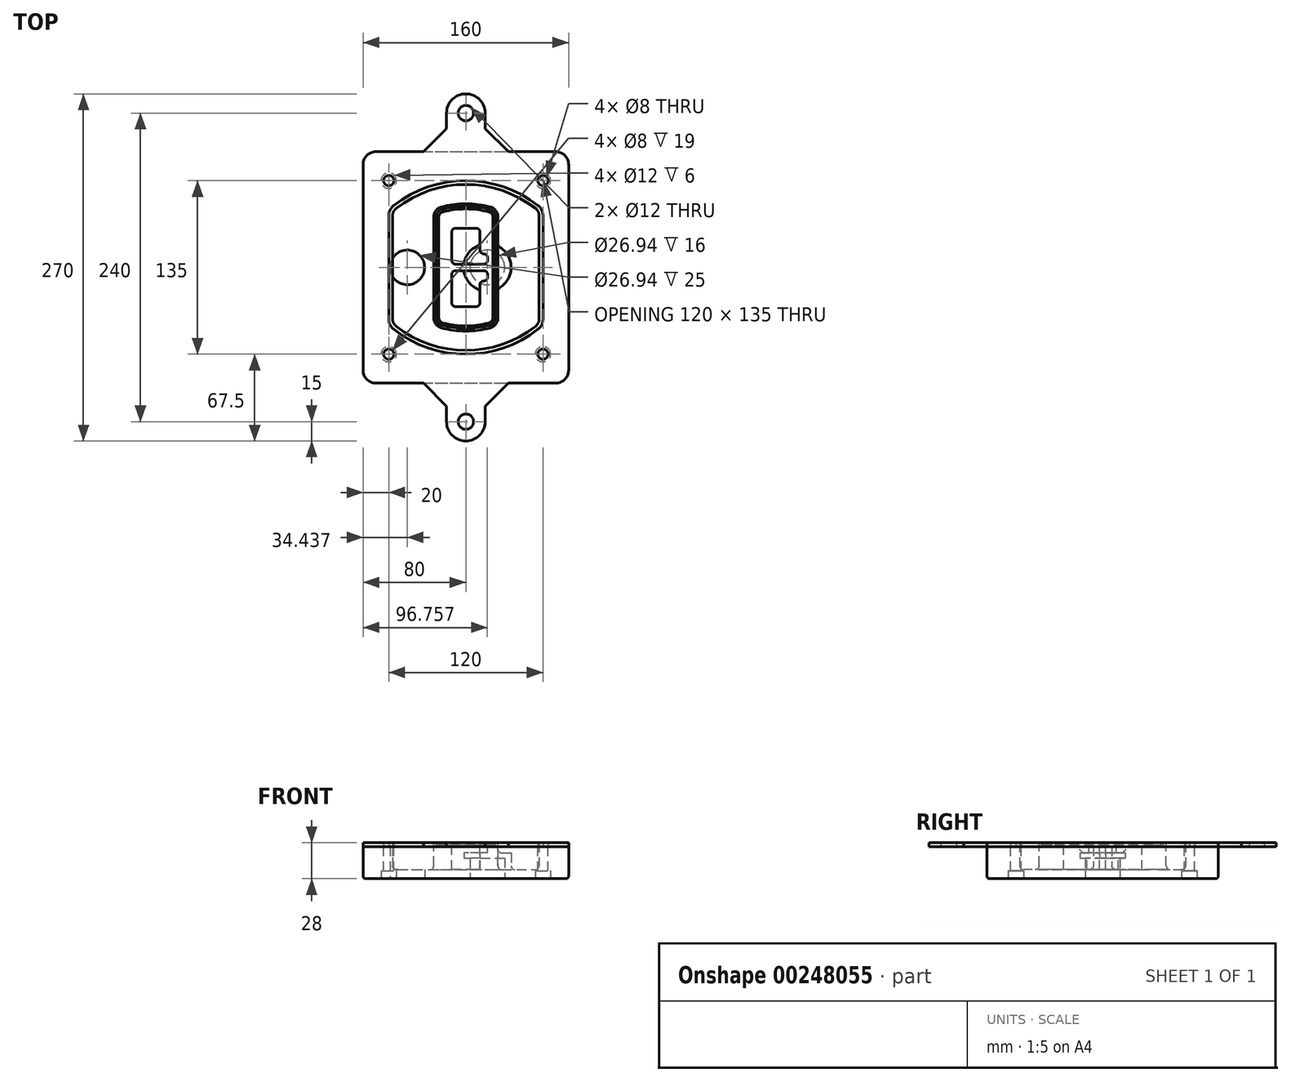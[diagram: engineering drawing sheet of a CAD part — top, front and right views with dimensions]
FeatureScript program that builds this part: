
annotation { "Feature Type Name" : "Feature", "Feature Type Description" : "" }
export const myFeature = defineFeature(function(context is Context, id is Id, definition is map)
    precondition{}
    {
        {
            var Q0;
            Q0=qCreatedBy(makeId("Top.planeOp"),FACE);
            var sketch = newSketch(context, id + "F0", { "sketchPlane" : qUnion([Q0])});
            skPoint(sketch, "E0.rect.middle", {"position": v(0, 0) * mm});
            skLineSegment(sketch, "E1.bottom", {"start": v(-70, -90) * mm, "end": v(70, -90) * mm});
            skLineSegment(sketch, "E1.top", {"start": v(-70, 90) * mm, "end": v(70, 90) * mm});
            skLineSegment(sketch, "E1.left", {"start": v(-80, -80) * mm, "end": v(-80, 80) * mm});
            skLineSegment(sketch, "E1.right", {"start": v(80, -80) * mm, "end": v(80, 80) * mm});
            skLineSegment(sketch, "E2", {"start": v(-80, 90) * mm, "end": v(80, -90) * mm, "construction": true});
            skLineSegment(sketch, "E3", {"start": v(80, 90) * mm, "end": v(-80, -90) * mm, "construction": true});
            skCircle(sketch, "E4", {"center": v(-60, 67.5) * mm, "radius": 4 * mm});
            skCircle(sketch, "E5", {"center": v(60, 67.5) * mm, "radius": 4 * mm});
            skCircle(sketch, "E6", {"center": v(60, -67.5) * mm, "radius": 4 * mm});
            skCircle(sketch, "E7", {"center": v(-60, -67.5) * mm, "radius": 4 * mm});
            skLineSegment(sketch, "E8", {"start": v(-60, 67.5) * mm, "end": v(60, 67.5) * mm, "construction": true});
            skLineSegment(sketch, "E9", {"start": v(60, 67.5) * mm, "end": v(60, -67.5) * mm, "construction": true});
            skLineSegment(sketch, "E10", {"start": v(60, -67.5) * mm, "end": v(-60, -67.5) * mm, "construction": true});
            skLineSegment(sketch, "E11", {"start": v(-60, -67.5) * mm, "end": v(-60, 67.5) * mm, "construction": true});
            skLineSegment(sketch, "E12", {"start": v(-60, 40.3) * mm, "end": v(-60, -40.3) * mm});
            skLineSegment(sketch, "E13", {"start": v(60, 40.3) * mm, "end": v(60, -40.3) * mm});
            skArc(sketch, "E14", {"start": v(56.15, 48.18) * mm, "mid": v(0, 67.5) * mm, "end": v(-56.15, 48.18) * mm});
            skArc(sketch, "E15", {"start": v(-56.15, -48.18) * mm, "mid": v(0, -67.5) * mm, "end": v(56.15, -48.18) * mm});
            skLineSegment(sketch, "E16", {"start": v(-60, 0) * mm, "end": v(60, 0) * mm, "construction": true});
            skPoint(sketch, "E17.visualSharp", {"position": v(-60, -45) * mm});
            skArc(sketch, "E17.filletArc", {"start": v(-60, -40.3) * mm, "mid": v(-58.99, -44.68) * mm, "end": v(-56.15, -48.18) * mm});
            skPoint(sketch, "E18.visualSharp", {"position": v(-60, 45) * mm});
            skArc(sketch, "E18.filletArc", {"start": v(-56.15, 48.18) * mm, "mid": v(-58.99, 44.68) * mm, "end": v(-60, 40.3) * mm});
            skPoint(sketch, "E19.visualSharp", {"position": v(60, 45) * mm});
            skArc(sketch, "E19.filletArc", {"start": v(60, 40.3) * mm, "mid": v(58.99, 44.68) * mm, "end": v(56.15, 48.18) * mm});
            skPoint(sketch, "E20.visualSharp", {"position": v(60, -45) * mm});
            skArc(sketch, "E20.filletArc", {"start": v(56.15, -48.18) * mm, "mid": v(58.99, -44.68) * mm, "end": v(60, -40.3) * mm});
            skPoint(sketch, "E21.visualSharp", {"position": v(-80, 90) * mm});
            skArc(sketch, "E21.filletArc", {"start": v(-70, 90) * mm, "mid": v(-77.07, 87.07) * mm, "end": v(-80, 80) * mm});
            skPoint(sketch, "E22.visualSharp", {"position": v(80, 90) * mm});
            skArc(sketch, "E22.filletArc", {"start": v(80, 80) * mm, "mid": v(77.07, 87.07) * mm, "end": v(70, 90) * mm});
            skPoint(sketch, "E23.visualSharp", {"position": v(80, -90) * mm});
            skArc(sketch, "E23.filletArc", {"start": v(70, -90) * mm, "mid": v(77.07, -87.07) * mm, "end": v(80, -80) * mm});
            skPoint(sketch, "E24.visualSharp", {"position": v(-80, -90) * mm});
            skArc(sketch, "E24.filletArc", {"start": v(-80, -80) * mm, "mid": v(-77.07, -87.07) * mm, "end": v(-70, -90) * mm});
            skArc(sketch, "E25.0", {"start": v(57, 40.3) * mm, "mid": v(56.3, 43.36) * mm, "end": v(54.3, 45.81) * mm});
            skLineSegment(sketch, "E25.1", {"start": v(57, 40.3) * mm, "end": v(57, -40.3) * mm});
            skArc(sketch, "E25.2", {"start": v(54.3, -45.81) * mm, "mid": v(56.3, -43.36) * mm, "end": v(57, -40.3) * mm});
            skArc(sketch, "E25.3", {"start": v(-54.3, -45.81) * mm, "mid": v(0, -64.5) * mm, "end": v(54.3, -45.81) * mm});
            skArc(sketch, "E25.4", {"start": v(-57, -40.3) * mm, "mid": v(-56.3, -43.36) * mm, "end": v(-54.3, -45.81) * mm});
            skArc(sketch, "E25.5", {"start": v(54.3, 45.81) * mm, "mid": v(0, 64.5) * mm, "end": v(-54.3, 45.81) * mm});
            skLineSegment(sketch, "E25.6", {"start": v(-57, 40.3) * mm, "end": v(-57, -40.3) * mm});
            skArc(sketch, "E25.7", {"start": v(-54.3, 45.81) * mm, "mid": v(-56.3, 43.36) * mm, "end": v(-57, 40.3) * mm});
            skArc(sketch, "E26.0", {"start": v(-58.62, 51.33) * mm, "mid": v(-62.58, 46.43) * mm, "end": v(-64, 40.3) * mm});
            skArc(sketch, "E26.1", {"start": v(58.62, 51.33) * mm, "mid": v(0, 71.5) * mm, "end": v(-58.62, 51.33) * mm});
            skArc(sketch, "E26.2", {"start": v(64, 40.3) * mm, "mid": v(62.58, 46.43) * mm, "end": v(58.62, 51.33) * mm});
            skLineSegment(sketch, "E26.3", {"start": v(64, 40.3) * mm, "end": v(64, -40.3) * mm});
            skArc(sketch, "E26.4", {"start": v(58.62, -51.33) * mm, "mid": v(62.58, -46.43) * mm, "end": v(64, -40.3) * mm});
            skLineSegment(sketch, "E26.5", {"start": v(-64, 40.3) * mm, "end": v(-64, -40.3) * mm});
            skArc(sketch, "E26.6", {"start": v(-58.62, -51.33) * mm, "mid": v(0, -71.5) * mm, "end": v(58.62, -51.33) * mm});
            skArc(sketch, "E26.7", {"start": v(-64, -40.3) * mm, "mid": v(-62.58, -46.43) * mm, "end": v(-58.62, -51.33) * mm});
            skSolve(sketch);
        }
        {
            var Q0;
            Q0=makeQuery(id+"F0.imprint","IMPRINT",FACE,{"disambiguationData":[TD([[makeQuery(id+"F0.imprint","IMPRINT",EDGE,{"derivedFrom":sQuery(id+"F0.wireOp",EDGE,"E1.bottom")}),1.0]])]});
            var Q1;
            Q1=makeQuery(id+"F0.imprint","IMPRINT",FACE,{"disambiguationData":[TD([[makeQuery(id+"F0.imprint","IMPRINT",EDGE,{"derivedFrom":sQuery(id+"F0.wireOp",EDGE,"E12")}),1.0]])]});
            var Q2;
            Q2=makeQuery(id+"F0.imprint","IMPRINT",FACE,{"disambiguationData":[TD([[makeQuery(id+"F0.imprint","IMPRINT",EDGE,{"derivedFrom":sQuery(id+"F0.wireOp",EDGE,"E25.0")}),1.0]])]});
            var Q3;
            Q3=makeQuery(id+"F0.imprint","IMPRINT",FACE,{"disambiguationData":[TD([[makeQuery(id+"F0.imprint","IMPRINT",EDGE,{"derivedFrom":sQuery(id+"F0.wireOp",EDGE,"E12")}),-1.0]])]});
            extrude(context, id + "F1", {"entities" : qUnion([Q0, Q1, Q2, Q3]), "oppositeDirection" : true, "depth" : 25 * mm});
        }
        {
            var Q0;
            Q0=makeQuery(id+"F0.imprint","IMPRINT",FACE,{"disambiguationData":[TD([[makeQuery(id+"F0.imprint","IMPRINT",EDGE,{"derivedFrom":sQuery(id+"F0.wireOp",EDGE,"E12")}),1.0]])]});
            extrude(context, id + "F2", {"entities" : qUnion([Q0]), "operationType" : NewBodyOperationType.ADD, "depth" : 3 * mm});
        }
        {
            var Q0;
            Q0=makeQuery(id+"F0.imprint","IMPRINT",FACE,{"disambiguationData":[TD([[makeQuery(id+"F0.imprint","IMPRINT",EDGE,{"derivedFrom":sQuery(id+"F0.wireOp",EDGE,"E25.0")}),1.0]])]});
            extrude(context, id + "F3", {"entities" : qUnion([Q0]), "operationType" : NewBodyOperationType.REMOVE, "oppositeDirection" : true, "depth" : 18 * mm});
        }
        {
            var Q0;
            Q0=makeQuery(id+"F2.opExtrude","CAP_FACE",FACE,{"disambiguationData":[OSD([sQuery(id+"F0.wireOp",EDGE,"E12"),sQuery(id+"F0.wireOp",EDGE,"E13"),sQuery(id+"F0.wireOp",EDGE,"E14"),sQuery(id+"F0.wireOp",EDGE,"E15"),sQuery(id+"F0.wireOp",EDGE,"E17.filletArc"),sQuery(id+"F0.wireOp",EDGE,"E18.filletArc"),sQuery(id+"F0.wireOp",EDGE,"E19.filletArc"),sQuery(id+"F0.wireOp",EDGE,"E20.filletArc"),sQuery(id+"F0.wireOp",EDGE,"E25.0"),sQuery(id+"F0.wireOp",EDGE,"E25.1"),sQuery(id+"F0.wireOp",EDGE,"E25.2"),sQuery(id+"F0.wireOp",EDGE,"E25.3"),sQuery(id+"F0.wireOp",EDGE,"E25.4"),sQuery(id+"F0.wireOp",EDGE,"E25.5"),sQuery(id+"F0.wireOp",EDGE,"E25.6"),sQuery(id+"F0.wireOp",EDGE,"E25.7")])],"isStart":false});
            var sketch = newSketch(context, id + "F4", { "sketchPlane" : qUnion([Q0])});
            skArc(sketch, "E27.0", {"start": v(-19.08, -46.97) * mm, "mid": v(0, -49.5) * mm, "end": v(19.08, -46.97) * mm});
            skArc(sketch, "E28.0", {"start": v(19.08, 46.97) * mm, "mid": v(0, 49.5) * mm, "end": v(-19.08, 46.97) * mm});
            skLineSegment(sketch, "E29", {"start": v(-25, 39.25) * mm, "end": v(-25, -39.25) * mm});
            skLineSegment(sketch, "E30", {"start": v(25, 39.25) * mm, "end": v(25, -39.25) * mm});
            skLineSegment(sketch, "E31", {"start": v(-25, 45.1) * mm, "end": v(25, 45.1) * mm, "construction": true});
            skLineSegment(sketch, "E32", {"start": v(-25, -45.1) * mm, "end": v(25, -45.1) * mm, "construction": true});
            skPoint(sketch, "E33.visualSharp", {"position": v(-25, 45.1) * mm});
            skArc(sketch, "E33.filletArc", {"start": v(-19.08, 46.97) * mm, "mid": v(-23.35, 44.11) * mm, "end": v(-25, 39.25) * mm});
            skPoint(sketch, "E34.visualSharp", {"position": v(25, 45.1) * mm});
            skArc(sketch, "E34.filletArc", {"start": v(25, 39.25) * mm, "mid": v(23.35, 44.11) * mm, "end": v(19.08, 46.97) * mm});
            skPoint(sketch, "E35.visualSharp", {"position": v(25, -45.1) * mm});
            skArc(sketch, "E35.filletArc", {"start": v(19.08, -46.97) * mm, "mid": v(23.35, -44.11) * mm, "end": v(25, -39.25) * mm});
            skPoint(sketch, "E36.visualSharp", {"position": v(-25, -45.1) * mm});
            skArc(sketch, "E36.filletArc", {"start": v(-25, -39.25) * mm, "mid": v(-23.35, -44.11) * mm, "end": v(-19.08, -46.97) * mm});
            skArc(sketch, "E37.0", {"start": v(54.3, 45.81) * mm, "mid": v(0, 64.5) * mm, "end": v(-54.3, 45.81) * mm});
            skArc(sketch, "E37.1", {"start": v(-54.3, 45.81) * mm, "mid": v(-56.3, 43.36) * mm, "end": v(-57, 40.3) * mm});
            skLineSegment(sketch, "E37.2", {"start": v(-57, 40.3) * mm, "end": v(-57, -40.3) * mm});
            skArc(sketch, "E37.3", {"start": v(-57, -40.3) * mm, "mid": v(-56.3, -43.36) * mm, "end": v(-54.3, -45.81) * mm});
            skArc(sketch, "E37.4", {"start": v(-54.3, -45.81) * mm, "mid": v(0, -64.5) * mm, "end": v(54.3, -45.81) * mm});
            skArc(sketch, "E37.5", {"start": v(54.3, -45.81) * mm, "mid": v(56.3, -43.36) * mm, "end": v(57, -40.3) * mm});
            skLineSegment(sketch, "E37.6", {"start": v(57, 40.3) * mm, "end": v(57, -40.3) * mm});
            skArc(sketch, "E37.7", {"start": v(57, 40.3) * mm, "mid": v(56.3, 43.36) * mm, "end": v(54.3, 45.81) * mm});
            skLineSegment(sketch, "E38.0", {"start": v(23, 39.25) * mm, "end": v(23, -39.25) * mm});
            skArc(sketch, "E38.1", {"start": v(18.56, -45.04) * mm, "mid": v(21.76, -42.9) * mm, "end": v(23, -39.25) * mm});
            skArc(sketch, "E38.2", {"start": v(-18.56, -45.04) * mm, "mid": v(0, -47.5) * mm, "end": v(18.56, -45.04) * mm});
            skArc(sketch, "E38.3", {"start": v(-23, -39.25) * mm, "mid": v(-21.76, -42.9) * mm, "end": v(-18.56, -45.04) * mm});
            skLineSegment(sketch, "E38.4", {"start": v(-23, 39.25) * mm, "end": v(-23, -39.25) * mm});
            skArc(sketch, "E38.5", {"start": v(23, 39.25) * mm, "mid": v(21.76, 42.9) * mm, "end": v(18.56, 45.04) * mm});
            skArc(sketch, "E38.6", {"start": v(-18.56, 45.04) * mm, "mid": v(-21.76, 42.9) * mm, "end": v(-23, 39.25) * mm});
            skArc(sketch, "E38.7", {"start": v(18.56, 45.04) * mm, "mid": v(0, 47.5) * mm, "end": v(-18.56, 45.04) * mm});
            skArc(sketch, "E39.0", {"start": v(21, 39.25) * mm, "mid": v(20.18, 41.68) * mm, "end": v(18.04, 43.1) * mm});
            skLineSegment(sketch, "E39.1", {"start": v(21, 39.25) * mm, "end": v(21, -39.25) * mm});
            skArc(sketch, "E39.2", {"start": v(18.04, -43.1) * mm, "mid": v(20.18, -41.68) * mm, "end": v(21, -39.25) * mm});
            skArc(sketch, "E39.3", {"start": v(-18.04, -43.1) * mm, "mid": v(0, -45.5) * mm, "end": v(18.04, -43.1) * mm});
            skArc(sketch, "E39.4", {"start": v(-21, -39.25) * mm, "mid": v(-20.18, -41.68) * mm, "end": v(-18.04, -43.1) * mm});
            skArc(sketch, "E39.5", {"start": v(18.04, 43.1) * mm, "mid": v(0, 45.5) * mm, "end": v(-18.04, 43.1) * mm});
            skLineSegment(sketch, "E39.6", {"start": v(-21, 39.25) * mm, "end": v(-21, -39.25) * mm});
            skArc(sketch, "E39.7", {"start": v(-18.04, 43.1) * mm, "mid": v(-20.18, 41.68) * mm, "end": v(-21, 39.25) * mm});
            skLineSegment(sketch, "E40", {"start": v(-25, 0) * mm, "end": v(25, 0) * mm, "construction": true});
            skLineSegment(sketch, "E41", {"start": v(-11, 5.5) * mm, "end": v(-11, 27.5) * mm});
            skLineSegment(sketch, "E42", {"start": v(-8, 30.5) * mm, "end": v(8, 30.5) * mm});
            skLineSegment(sketch, "E43", {"start": v(11, 27.5) * mm, "end": v(11, 13.5) * mm});
            skLineSegment(sketch, "E44", {"start": v(14, 10.5) * mm, "end": v(14, 10.5) * mm});
            skLineSegment(sketch, "E45", {"start": v(17, 7.5) * mm, "end": v(17, 5.5) * mm});
            skLineSegment(sketch, "E46", {"start": v(14, 2.5) * mm, "end": v(-8, 2.5) * mm});
            skPoint(sketch, "E47.visualSharp", {"position": v(-11, 30.5) * mm});
            skArc(sketch, "E47.filletArc", {"start": v(-8, 30.5) * mm, "mid": v(-10.12, 29.62) * mm, "end": v(-11, 27.5) * mm});
            skPoint(sketch, "E48.visualSharp", {"position": v(11, 30.5) * mm});
            skArc(sketch, "E48.filletArc", {"start": v(11, 27.5) * mm, "mid": v(10.12, 29.62) * mm, "end": v(8, 30.5) * mm});
            skPoint(sketch, "E49.visualSharp", {"position": v(11, 10.5) * mm});
            skArc(sketch, "E49.filletArc", {"start": v(11, 13.5) * mm, "mid": v(11.88, 11.38) * mm, "end": v(14, 10.5) * mm});
            skPoint(sketch, "E50.visualSharp", {"position": v(17, 10.5) * mm});
            skArc(sketch, "E50.filletArc", {"start": v(17, 7.5) * mm, "mid": v(16.12, 9.62) * mm, "end": v(14, 10.5) * mm});
            skPoint(sketch, "E51.visualSharp", {"position": v(17, 2.5) * mm});
            skArc(sketch, "E51.filletArc", {"start": v(14, 2.5) * mm, "mid": v(16.12, 3.38) * mm, "end": v(17, 5.5) * mm});
            skPoint(sketch, "E52.visualSharp", {"position": v(-11, 2.5) * mm});
            skArc(sketch, "E52.filletArc", {"start": v(-11, 5.5) * mm, "mid": v(-10.12, 3.38) * mm, "end": v(-8, 2.5) * mm});
            skLineSegment(sketch, "E53.0.MirrorCS", {"start": v(14, -2.5) * mm, "end": v(-8, -2.5) * mm});
            skArc(sketch, "E54.0.MirrorCS", {"start": v(-11, -5.5) * mm, "mid": v(-10.12, -3.38) * mm, "end": v(-8, -2.5) * mm});
            skLineSegment(sketch, "E55.0.MirrorCS", {"start": v(-11, -5.5) * mm, "end": v(-11, -27.5) * mm});
            skArc(sketch, "E56.0.MirrorCS", {"start": v(-8, -30.5) * mm, "mid": v(-10.12, -29.62) * mm, "end": v(-11, -27.5) * mm});
            skLineSegment(sketch, "E57.0.MirrorCS", {"start": v(-8, -30.5) * mm, "end": v(8, -30.5) * mm});
            skArc(sketch, "E58.0.MirrorCS", {"start": v(11, -27.5) * mm, "mid": v(10.12, -29.62) * mm, "end": v(8, -30.5) * mm});
            skLineSegment(sketch, "E59.0.MirrorCS", {"start": v(11, -27.5) * mm, "end": v(11, -13.5) * mm});
            skArc(sketch, "E60.0.MirrorCS", {"start": v(11, -13.5) * mm, "mid": v(11.88, -11.38) * mm, "end": v(14, -10.5) * mm});
            skArc(sketch, "E61.0.MirrorCS", {"start": v(17, -7.5) * mm, "mid": v(16.12, -9.62) * mm, "end": v(14, -10.5) * mm});
            skLineSegment(sketch, "E62.0.MirrorCS", {"start": v(17, -7.5) * mm, "end": v(17, -5.5) * mm});
            skArc(sketch, "E63.0.MirrorCS", {"start": v(14, -2.5) * mm, "mid": v(16.12, -3.38) * mm, "end": v(17, -5.5) * mm});
            skSolve(sketch);
        }
        {
            var Q0;
            Q0=makeQuery(id+"F4.imprint","IMPRINT",FACE,{"disambiguationData":[TD([[makeQuery(id+"F4.imprint","IMPRINT",EDGE,{"derivedFrom":sQuery(id+"F4.wireOp",EDGE,"E27.0")}),1.0]])]});
            var Q1;
            Q1=makeQuery(id+"F4.imprint","IMPRINT",FACE,{"disambiguationData":[TD([[makeQuery(id+"F4.imprint","IMPRINT",EDGE,{"derivedFrom":sQuery(id+"F4.wireOp",EDGE,"E38.0")}),-1.0]])]});
            var Q2;
            Q2=makeQuery(id+"F4.imprint","IMPRINT",FACE,{"disambiguationData":[TD([[makeQuery(id+"F4.imprint","IMPRINT",EDGE,{"derivedFrom":sQuery(id+"F4.wireOp",EDGE,"E39.0")}),1.0]])]});
            extrude(context, id + "F5", {"entities" : qUnion([Q0, Q1, Q2]), "operationType" : NewBodyOperationType.ADD, "endBound" : BoundingType.UP_TO_NEXT, "oppositeDirection" : true, "depth" : 25 * mm});
        }
        {
            var Q0;
            Q0=makeQuery(id+"F4.imprint","IMPRINT",FACE,{"disambiguationData":[TD([[makeQuery(id+"F4.imprint","IMPRINT",EDGE,{"derivedFrom":sQuery(id+"F4.wireOp",EDGE,"E38.0")}),-1.0]])]});
            extrude(context, id + "F6", {"entities" : qUnion([Q0]), "operationType" : NewBodyOperationType.REMOVE, "oppositeDirection" : true, "depth" : 2 * mm});
        }
        {
            var Q0;
            Q0=makeQuery(id+"F1.opExtrude","CAP_FACE",FACE,{"disambiguationData":[OSD([sQuery(id+"F0.wireOp",EDGE,"E1.bottom"),sQuery(id+"F0.wireOp",EDGE,"E1.top"),sQuery(id+"F0.wireOp",EDGE,"E1.left"),sQuery(id+"F0.wireOp",EDGE,"E1.right"),sQuery(id+"F0.wireOp",EDGE,"E4"),sQuery(id+"F0.wireOp",EDGE,"E5"),sQuery(id+"F0.wireOp",EDGE,"E6"),sQuery(id+"F0.wireOp",EDGE,"E7"),sQuery(id+"F0.wireOp",EDGE,"E21.filletArc"),sQuery(id+"F0.wireOp",EDGE,"E22.filletArc"),sQuery(id+"F0.wireOp",EDGE,"E23.filletArc"),sQuery(id+"F0.wireOp",EDGE,"E24.filletArc")])],"isStart":false});
            var sketch = newSketch(context, id + "F7", { "sketchPlane" : qUnion([Q0])});
            skCircle(sketch, "E64", {"center": v(16.76, 0) * mm, "radius": 13.47 * mm});
            skCircle(sketch, "E65", {"center": v(-45.56, 0) * mm, "radius": 13.47 * mm});
            skLineSegment(sketch, "E66", {"start": v(80, 0) * mm, "end": v(-80, 0) * mm});
            skCircle(sketch, "E67", {"center": v(16.76, 0) * mm, "radius": 18.47 * mm});
            skCircle(sketch, "E68", {"center": v(60, -67.5) * mm, "radius": 6 * mm});
            skCircle(sketch, "E69", {"center": v(-60, -67.5) * mm, "radius": 6 * mm});
            skCircle(sketch, "E70", {"center": v(-60, 67.5) * mm, "radius": 6 * mm});
            skCircle(sketch, "E71", {"center": v(60, 67.5) * mm, "radius": 6 * mm});
            skSolve(sketch);
        }
        {
            var Q0;
            {var subQ1=sQuery(id+"F7.wireOp",EDGE,"E66");var subQ4=sQuery(id+"F7.wireOp",EDGE,"E64");var subQ6=makeQuery(id+"F7.imprint","INTERSECT",VERTEX,{"disambiguationData":[OD(0.0)],"derivedFrom":[subQ4,subQ1]});Q0=makeQuery(id+"F7.imprint","IMPRINT",FACE,{"disambiguationData":[TD([[makeQuery(id+"F7.imprint","IMPRINT",EDGE,{"disambiguationData":[TD([[subQ6,-1.0]])],"derivedFrom":subQ4}),-1.0]])]});}
            var Q1;
            {var subQ0=sQuery(id+"F7.wireOp",EDGE,"E66");var subQ1=sQuery(id+"F7.wireOp",EDGE,"E64");var subQ3=makeQuery(id+"F7.imprint","INTERSECT",VERTEX,{"disambiguationData":[OD(0.0)],"derivedFrom":[subQ1,subQ0]});Q1=makeQuery(id+"F7.imprint","IMPRINT",FACE,{"disambiguationData":[TD([[makeQuery(id+"F7.imprint","IMPRINT",EDGE,{"disambiguationData":[TD([[subQ3,-1.0]])],"derivedFrom":subQ1}),1.0]])]});}
            var Q2;
            {var subQ0=sQuery(id+"F7.wireOp",EDGE,"E66");var subQ1=sQuery(id+"F7.wireOp",EDGE,"E64");var subQ3=makeQuery(id+"F7.imprint","INTERSECT",VERTEX,{"disambiguationData":[OD(0.0)],"derivedFrom":[subQ1,subQ0]});Q2=makeQuery(id+"F7.imprint","IMPRINT",FACE,{"disambiguationData":[TD([[makeQuery(id+"F7.imprint","IMPRINT",EDGE,{"disambiguationData":[TD([[subQ3,1.0]])],"derivedFrom":subQ1}),1.0]])]});}
            var Q3;
            {var subQ1=sQuery(id+"F7.wireOp",EDGE,"E66");var subQ4=sQuery(id+"F7.wireOp",EDGE,"E64");var subQ6=makeQuery(id+"F7.imprint","INTERSECT",VERTEX,{"disambiguationData":[OD(0.0)],"derivedFrom":[subQ4,subQ1]});Q3=makeQuery(id+"F7.imprint","IMPRINT",FACE,{"disambiguationData":[TD([[makeQuery(id+"F7.imprint","IMPRINT",EDGE,{"disambiguationData":[TD([[subQ6,1.0]])],"derivedFrom":subQ4}),-1.0]])]});}
            extrude(context, id + "F8", {"entities" : qUnion([Q0, Q1, Q2, Q3]), "operationType" : NewBodyOperationType.ADD, "oppositeDirection" : true, "depth" : 20 * mm});
        }
        {
            var Q0;
            {var subQ0=sQuery(id+"F7.wireOp",EDGE,"E66");var subQ1=sQuery(id+"F7.wireOp",EDGE,"E64");var subQ3=makeQuery(id+"F7.imprint","INTERSECT",VERTEX,{"disambiguationData":[OD(0.0)],"derivedFrom":[subQ1,subQ0]});Q0=makeQuery(id+"F7.imprint","IMPRINT",FACE,{"disambiguationData":[TD([[makeQuery(id+"F7.imprint","IMPRINT",EDGE,{"disambiguationData":[TD([[subQ3,-1.0]])],"derivedFrom":subQ1}),1.0]])]});}
            var Q1;
            {var subQ0=sQuery(id+"F7.wireOp",EDGE,"E66");var subQ1=sQuery(id+"F7.wireOp",EDGE,"E64");var subQ3=makeQuery(id+"F7.imprint","INTERSECT",VERTEX,{"disambiguationData":[OD(0.0)],"derivedFrom":[subQ1,subQ0]});Q1=makeQuery(id+"F7.imprint","IMPRINT",FACE,{"disambiguationData":[TD([[makeQuery(id+"F7.imprint","IMPRINT",EDGE,{"disambiguationData":[TD([[subQ3,1.0]])],"derivedFrom":subQ1}),1.0]])]});}
            extrude(context, id + "F9", {"entities" : qUnion([Q0, Q1]), "operationType" : NewBodyOperationType.REMOVE, "oppositeDirection" : true, "depth" : 16 * mm});
        }
        {
            var Q0;
            {var subQ0=sQuery(id+"F7.wireOp",EDGE,"E66");var subQ1=sQuery(id+"F7.wireOp",EDGE,"E65");var subQ3=makeQuery(id+"F7.imprint","INTERSECT",VERTEX,{"disambiguationData":[OD(0.0)],"derivedFrom":[subQ1,subQ0]});Q0=makeQuery(id+"F7.imprint","IMPRINT",FACE,{"disambiguationData":[TD([[makeQuery(id+"F7.imprint","IMPRINT",EDGE,{"disambiguationData":[TD([[subQ3,-1.0]])],"derivedFrom":subQ1}),1.0]])]});}
            var Q1;
            {var subQ0=sQuery(id+"F7.wireOp",EDGE,"E66");var subQ1=sQuery(id+"F7.wireOp",EDGE,"E65");var subQ3=makeQuery(id+"F7.imprint","INTERSECT",VERTEX,{"disambiguationData":[OD(0.0)],"derivedFrom":[subQ1,subQ0]});Q1=makeQuery(id+"F7.imprint","IMPRINT",FACE,{"disambiguationData":[TD([[makeQuery(id+"F7.imprint","IMPRINT",EDGE,{"disambiguationData":[TD([[subQ3,1.0]])],"derivedFrom":subQ1}),1.0]])]});}
            extrude(context, id + "F10", {"entities" : qUnion([Q0, Q1]), "operationType" : NewBodyOperationType.REMOVE, "oppositeDirection" : true, "depth" : 25 * mm});
        }
        {
            var Q0;
            Q0=makeQuery(id+"F7.imprint","IMPRINT",FACE,{"disambiguationData":[TD([[makeQuery(id+"F7.imprint","IMPRINT",EDGE,{"derivedFrom":sQuery(id+"F7.wireOp",EDGE,"E68")}),1.0]])]});
            var Q1;
            Q1=makeQuery(id+"F7.imprint","IMPRINT",FACE,{"disambiguationData":[TD([[makeQuery(id+"F7.imprint","IMPRINT",EDGE,{"derivedFrom":makeQuery(id+"F1.opExtrude","CAP_EDGE",EDGE,{"disambiguationData":[OSD([sQuery(id+"F0.wireOp",EDGE,"E5")])],"isStart":false})}),-1.0]])]});
            var Q2;
            Q2=makeQuery(id+"F7.imprint","IMPRINT",FACE,{"disambiguationData":[TD([[makeQuery(id+"F7.imprint","IMPRINT",EDGE,{"derivedFrom":sQuery(id+"F7.wireOp",EDGE,"E69")}),1.0]])]});
            var Q3;
            Q3=makeQuery(id+"F7.imprint","IMPRINT",FACE,{"disambiguationData":[TD([[makeQuery(id+"F7.imprint","IMPRINT",EDGE,{"derivedFrom":makeQuery(id+"F1.opExtrude","CAP_EDGE",EDGE,{"disambiguationData":[OSD([sQuery(id+"F0.wireOp",EDGE,"E4")])],"isStart":false})}),-1.0]])]});
            var Q4;
            Q4=makeQuery(id+"F7.imprint","IMPRINT",FACE,{"disambiguationData":[TD([[makeQuery(id+"F7.imprint","IMPRINT",EDGE,{"derivedFrom":sQuery(id+"F7.wireOp",EDGE,"E70")}),1.0]])]});
            var Q5;
            Q5=makeQuery(id+"F7.imprint","IMPRINT",FACE,{"disambiguationData":[TD([[makeQuery(id+"F7.imprint","IMPRINT",EDGE,{"derivedFrom":makeQuery(id+"F1.opExtrude","CAP_EDGE",EDGE,{"disambiguationData":[OSD([sQuery(id+"F0.wireOp",EDGE,"E7")])],"isStart":false})}),-1.0]])]});
            var Q6;
            Q6=makeQuery(id+"F7.imprint","IMPRINT",FACE,{"disambiguationData":[TD([[makeQuery(id+"F7.imprint","IMPRINT",EDGE,{"derivedFrom":sQuery(id+"F7.wireOp",EDGE,"E71")}),1.0]])]});
            var Q7;
            Q7=makeQuery(id+"F7.imprint","IMPRINT",FACE,{"disambiguationData":[TD([[makeQuery(id+"F7.imprint","IMPRINT",EDGE,{"derivedFrom":makeQuery(id+"F1.opExtrude","CAP_EDGE",EDGE,{"disambiguationData":[OSD([sQuery(id+"F0.wireOp",EDGE,"E6")])],"isStart":false})}),-1.0]])]});
            extrude(context, id + "F11", {"entities" : qUnion([Q0, Q1, Q2, Q3, Q4, Q5, Q6, Q7]), "operationType" : NewBodyOperationType.REMOVE, "oppositeDirection" : true, "depth" : 6 * mm});
        }
        {
            var Q0;
            Q0=makeQuery(id+"F9.boolean.opBoolean","COPY",FACE,{"derivedFrom":makeQuery(id+"F9.opExtrude","CAP_FACE",FACE,{"disambiguationData":[OSD([sQuery(id+"F7.wireOp",EDGE,"E64")])],"isStart":false})});
            var sketch = newSketch(context, id + "F12", { "sketchPlane" : qUnion([Q0])});
            skArc(sketch, "E72.0", {"start": v(11, 17.55) * mm, "mid": v(2.57, 11.82) * mm, "end": v(-1.54, 2.5) * mm});
            skArc(sketch, "E72.1", {"start": v(-1.54, -2.5) * mm, "mid": v(2.57, -11.82) * mm, "end": v(11, -17.55) * mm});
            skLineSegment(sketch, "E73", {"start": v(-1.54, -2.5) * mm, "end": v(14, -2.5) * mm});
            skLineSegment(sketch, "E74.0", {"start": v(14, 2.5) * mm, "end": v(-1.54, 2.5) * mm});
            skArc(sketch, "E74.1", {"start": v(14, 2.5) * mm, "mid": v(16.12, 3.38) * mm, "end": v(17, 5.5) * mm});
            skLineSegment(sketch, "E74.2", {"start": v(17, 7.5) * mm, "end": v(17, 5.5) * mm});
            skArc(sketch, "E74.3", {"start": v(17, 7.5) * mm, "mid": v(16.12, 9.62) * mm, "end": v(14, 10.5) * mm});
            skArc(sketch, "E74.4", {"start": v(11, 13.5) * mm, "mid": v(11.88, 11.38) * mm, "end": v(14, 10.5) * mm});
            skLineSegment(sketch, "E74.5", {"start": v(11, 17.55) * mm, "end": v(11, 13.5) * mm});
            skLineSegment(sketch, "E74.7", {"start": v(14, -2.5) * mm, "end": v(-1.54, -2.5) * mm});
            skArc(sketch, "E74.8", {"start": v(14, -2.5) * mm, "mid": v(16.12, -3.38) * mm, "end": v(17, -5.5) * mm});
            skLineSegment(sketch, "E74.9", {"start": v(17, -7.5) * mm, "end": v(17, -5.5) * mm});
            skArc(sketch, "E74.10", {"start": v(17, -7.5) * mm, "mid": v(16.12, -9.62) * mm, "end": v(14, -10.5) * mm});
            skArc(sketch, "E74.11", {"start": v(11, -13.5) * mm, "mid": v(11.88, -11.38) * mm, "end": v(14, -10.5) * mm});
            skLineSegment(sketch, "E74.12", {"start": v(11, -17.55) * mm, "end": v(11, -13.5) * mm});
            skPoint(sketch, "E75.orphan", {"position": v(11, -27.5) * mm});
            skPoint(sketch, "E76.orphan", {"position": v(-8, -2.5) * mm});
            skPoint(sketch, "E77.orphan", {"position": v(-8, 2.5) * mm});
            skPoint(sketch, "E78.orphan", {"position": v(11, 27.5) * mm});
            skSolve(sketch);
        }
        {
            var Q0;
            {var subQ7=sQuery(id+"F12.wireOp",EDGE,"E72.0");var subQ14=sQuery(id+"F12.wireOp",EDGE,"E72.1");var subQ16=sQuery(id+"F12.wireOp",EDGE,"E74.1");var subQ18=sQuery(id+"F12.wireOp",EDGE,"E74.8");Q0=qUnion([makeQuery(id+"F12.imprint","IMPRINT",FACE,{"disambiguationData":[TD([[makeQuery(id+"F12.imprint","IMPRINT",EDGE,{"derivedFrom":subQ7}),1.0]])]}),makeQuery(id+"F12.imprint","IMPRINT",FACE,{"disambiguationData":[TD([[makeQuery(id+"F12.imprint","IMPRINT",EDGE,{"derivedFrom":subQ14}),1.0]])]}),makeQuery(id+"F12.imprint","IMPRINT",FACE,{"disambiguationData":[TD([[makeQuery(id+"F12.imprint","IMPRINT",EDGE,{"derivedFrom":subQ16}),1.0]])]}),makeQuery(id+"F12.imprint","IMPRINT",FACE,{"disambiguationData":[TD([[makeQuery(id+"F12.imprint","IMPRINT",EDGE,{"derivedFrom":subQ18}),-1.0]])]})]);}
            var Q1;
            Q1=makeQuery(id+"F5.boolean.opBoolean","SPLIT",FACE,{"disambiguationData":[TD([makeQuery(id+"F5.opExtrude","SWEPT_FACE",FACE,{"disambiguationData":[OSD([sQuery(id+"F4.wireOp",EDGE,"E41")])]})])],"derivedFrom":makeQuery(id+"F3.boolean.opBoolean","COPY",FACE,{"derivedFrom":makeQuery(id+"F3.opExtrude","CAP_FACE",FACE,{"disambiguationData":[OSD([sQuery(id+"F0.wireOp",EDGE,"E25.0"),sQuery(id+"F0.wireOp",EDGE,"E25.1"),sQuery(id+"F0.wireOp",EDGE,"E25.2"),sQuery(id+"F0.wireOp",EDGE,"E25.3"),sQuery(id+"F0.wireOp",EDGE,"E25.4"),sQuery(id+"F0.wireOp",EDGE,"E25.5"),sQuery(id+"F0.wireOp",EDGE,"E25.6"),sQuery(id+"F0.wireOp",EDGE,"E25.7")])],"isStart":false})})});
            extrude(context, id + "F13", {"entities" : qUnion([Q0]), "operationType" : NewBodyOperationType.REMOVE, "endBound" : BoundingType.UP_TO_SURFACE, "endBoundEntityFace" : qUnion([Q1]), "depth" : 25 * mm});
        }
        {
            var Q0;
            Q0=makeQuery(id+"F3.boolean.opBoolean","COPY",EDGE,{"derivedFrom":makeQuery(id+"F3.opExtrude","CAP_EDGE",EDGE,{"disambiguationData":[OSD([sQuery(id+"F0.wireOp",EDGE,"E25.6")])],"isStart":false})});
            var Q1;
            Q1=makeQuery(id+"F8.boolean.opBoolean","INTERSECT",EDGE,{"derivedFrom":[makeQuery(id+"F5.opExtrude","SWEPT_FACE",FACE,{"disambiguationData":[OSD([sQuery(id+"F4.wireOp",EDGE,"E30")])]}),makeQuery(id+"F8.opExtrude","CAP_FACE",FACE,{"disambiguationData":[OSD([sQuery(id+"F7.wireOp",EDGE,"E67")])],"isStart":false})]});
            var Q2;
            Q2=makeQuery(id+"F8.boolean.opBoolean","INTERSECT",EDGE,{"disambiguationData":[OD(1.0)],"derivedFrom":[makeQuery(id+"F5.opExtrude","SWEPT_FACE",FACE,{"disambiguationData":[OSD([sQuery(id+"F4.wireOp",EDGE,"E30")])]}),makeQuery(id+"F8.opExtrude","SWEPT_FACE",FACE,{"disambiguationData":[OSD([sQuery(id+"F7.wireOp",EDGE,"E67")])]})]});
            var Q3;
            {var subQ0=sQuery(id+"F4.wireOp",EDGE,"E30");Q3=makeQuery(id+"F8.boolean.opBoolean","SPLIT",EDGE,{"disambiguationData":[TD([makeQuery(id+"F5.opExtrude","SWEPT_FACE",FACE,{"disambiguationData":[OSD([sQuery(id+"F4.wireOp",EDGE,"E35.filletArc")])]})])],"derivedFrom":makeQuery(id+"F5.opExtrude","CAP_EDGE",EDGE,{"disambiguationData":[OSD([subQ0])],"isStart":false})});}
            var Q4;
            {var subQ0=sQuery(id+"F0.wireOp",EDGE,"E25.7");var subQ1=sQuery(id+"F0.wireOp",EDGE,"E25.1");var subQ2=sQuery(id+"F0.wireOp",EDGE,"E25.6");var subQ3=sQuery(id+"F0.wireOp",EDGE,"E25.5");var subQ4=sQuery(id+"F0.wireOp",EDGE,"E25.4");var subQ5=sQuery(id+"F0.wireOp",EDGE,"E25.0");var subQ6=sQuery(id+"F0.wireOp",EDGE,"E25.2");var subQ7=sQuery(id+"F0.wireOp",EDGE,"E25.3");Q4=makeQuery(id+"F8.boolean.opBoolean","INTERSECT",EDGE,{"derivedFrom":[makeQuery(id+"F5.boolean.opBoolean","SPLIT",FACE,{"disambiguationData":[TD([makeQuery(id+"F2.opExtrude","SWEPT_FACE",FACE,{"disambiguationData":[OSD([subQ5])]})])],"derivedFrom":makeQuery(id+"F3.boolean.opBoolean","COPY",FACE,{"derivedFrom":makeQuery(id+"F3.opExtrude","CAP_FACE",FACE,{"disambiguationData":[OSD([subQ5,subQ1,subQ6,subQ7,subQ4,subQ3,subQ2,subQ0])],"isStart":false})})}),makeQuery(id+"F8.opExtrude","SWEPT_FACE",FACE,{"disambiguationData":[OSD([sQuery(id+"F7.wireOp",EDGE,"E67")])]})]});}
            var Q5;
            Q5=makeQuery(id+"F8.boolean.opBoolean","INTERSECT",EDGE,{"disambiguationData":[OD(0.0)],"derivedFrom":[makeQuery(id+"F5.opExtrude","SWEPT_FACE",FACE,{"disambiguationData":[OSD([sQuery(id+"F4.wireOp",EDGE,"E30")])]}),makeQuery(id+"F8.opExtrude","SWEPT_FACE",FACE,{"disambiguationData":[OSD([sQuery(id+"F7.wireOp",EDGE,"E67")])]})]});
            fillet(context, id + "F14", {"entities" : qUnion([Q0, Q1, Q2, Q3, Q4, Q5]), "radius" : 3 * mm, "tangentPropagation" : true, "allowEdgeOverflow" : false});
        }
        {
            var Q0;
            Q0=makeQuery(id+"F1.opExtrude","CAP_EDGE",EDGE,{"disambiguationData":[OSD([sQuery(id+"F0.wireOp",EDGE,"E1.bottom")])],"isStart":false});
            fillet(context, id + "F15", {"entities" : qUnion([Q0]), "radius" : 2 * mm, "tangentPropagation" : true, "allowEdgeOverflow" : false});
        }
        {
            var Q0;
            {var subQ0=sQuery(id+"F0.wireOp",EDGE,"E22.filletArc");var subQ1=sQuery(id+"F0.wireOp",EDGE,"E7");var subQ2=sQuery(id+"F0.wireOp",EDGE,"E6");var subQ3=sQuery(id+"F0.wireOp",EDGE,"E5");var subQ4=sQuery(id+"F0.wireOp",EDGE,"E4");var subQ5=sQuery(id+"F0.wireOp",EDGE,"E1.bottom");var subQ6=sQuery(id+"F0.wireOp",EDGE,"E21.filletArc");var subQ7=sQuery(id+"F0.wireOp",EDGE,"E1.top");var subQ8=sQuery(id+"F0.wireOp",EDGE,"E1.left");var subQ9=sQuery(id+"F0.wireOp",EDGE,"E1.right");var subQ10=sQuery(id+"F0.wireOp",EDGE,"E23.filletArc");var subQ11=sQuery(id+"F0.wireOp",EDGE,"E24.filletArc");Q0=makeQuery(id+"F2.boolean.opBoolean","SPLIT",FACE,{"disambiguationData":[TD([makeQuery(id+"F1.opExtrude","SWEPT_FACE",FACE,{"disambiguationData":[OSD([subQ5])]})])],"derivedFrom":makeQuery(id+"F1.opExtrude","CAP_FACE",FACE,{"disambiguationData":[OSD([subQ5,subQ7,subQ8,subQ9,subQ4,subQ3,subQ2,subQ1,subQ6,subQ0,subQ10,subQ11])],"isStart":true})});}
            var sketch = newSketch(context, id + "F16", { "sketchPlane" : qUnion([Q0])});
            skLineSegment(sketch, "E79", {"start": v(0, 90) * mm, "end": v(0, 120) * mm, "construction": true});
            skCircle(sketch, "E80", {"center": v(0, 120) * mm, "radius": 6 * mm});
            skArc(sketch, "E81", {"start": v(15, 120) * mm, "mid": v(0, 135) * mm, "end": v(-15, 120) * mm});
            skLineSegment(sketch, "E82", {"start": v(-15, 120) * mm, "end": v(-15, 108) * mm});
            skLineSegment(sketch, "E83", {"start": v(-15, 108) * mm, "end": v(-33, 90) * mm});
            skLineSegment(sketch, "E84", {"start": v(-33, 90) * mm, "end": v(33, 90) * mm});
            skLineSegment(sketch, "E85", {"start": v(15, 120) * mm, "end": v(15, 108) * mm});
            skLineSegment(sketch, "E86", {"start": v(15, 108) * mm, "end": v(33, 90) * mm});
            skLineSegment(sketch, "E87.0", {"start": v(-80, -80) * mm, "end": v(-80, 80) * mm});
            skArc(sketch, "E87.1", {"start": v(-70, 90) * mm, "mid": v(-77.07, 87.07) * mm, "end": v(-80, 80) * mm});
            skLineSegment(sketch, "E87.2", {"start": v(-70, 90) * mm, "end": v(70, 90) * mm});
            skArc(sketch, "E87.3", {"start": v(80, 80) * mm, "mid": v(77.07, 87.07) * mm, "end": v(70, 90) * mm});
            skLineSegment(sketch, "E87.4", {"start": v(80, -80) * mm, "end": v(80, 80) * mm});
            skArc(sketch, "E87.5", {"start": v(70, -90) * mm, "mid": v(77.07, -87.07) * mm, "end": v(80, -80) * mm});
            skLineSegment(sketch, "E87.6", {"start": v(-70, -90) * mm, "end": v(70, -90) * mm});
            skArc(sketch, "E87.7", {"start": v(-80, -80) * mm, "mid": v(-77.07, -87.07) * mm, "end": v(-70, -90) * mm});
            skCircle(sketch, "E87.8", {"center": v(-60, -67.5) * mm, "radius": 4 * mm});
            skCircle(sketch, "E87.9", {"center": v(-60, 67.5) * mm, "radius": 4 * mm});
            skCircle(sketch, "E87.10", {"center": v(60, 67.5) * mm, "radius": 4 * mm});
            skCircle(sketch, "E87.11", {"center": v(60, -67.5) * mm, "radius": 4 * mm});
            skArc(sketch, "E87.12", {"start": v(-56.15, -48.18) * mm, "mid": v(0, -67.5) * mm, "end": v(56.15, -48.18) * mm});
            skArc(sketch, "E87.13", {"start": v(-60, -40.3) * mm, "mid": v(-58.99, -44.68) * mm, "end": v(-56.15, -48.18) * mm});
            skLineSegment(sketch, "E87.14", {"start": v(-60, 40.3) * mm, "end": v(-60, -40.3) * mm});
            skArc(sketch, "E87.15", {"start": v(-56.15, 48.18) * mm, "mid": v(-58.99, 44.68) * mm, "end": v(-60, 40.3) * mm});
            skArc(sketch, "E87.16", {"start": v(56.15, 48.18) * mm, "mid": v(0, 67.5) * mm, "end": v(-56.15, 48.18) * mm});
            skArc(sketch, "E87.17", {"start": v(60, 40.3) * mm, "mid": v(58.99, 44.68) * mm, "end": v(56.15, 48.18) * mm});
            skLineSegment(sketch, "E87.18", {"start": v(60, 40.3) * mm, "end": v(60, -40.3) * mm});
            skArc(sketch, "E87.19", {"start": v(56.15, -48.18) * mm, "mid": v(58.99, -44.68) * mm, "end": v(60, -40.3) * mm});
            skLineSegment(sketch, "E88", {"start": v(-80, 0) * mm, "end": v(80, 0) * mm, "construction": true});
            skArc(sketch, "E89.MirrorCS", {"start": v(15, -120) * mm, "mid": v(0, -135) * mm, "end": v(-15, -120) * mm});
            skLineSegment(sketch, "E90.MirrorCS", {"start": v(-15, -108) * mm, "end": v(-33, -90) * mm});
            skLineSegment(sketch, "E91.MirrorCS", {"start": v(15, -108) * mm, "end": v(33, -90) * mm});
            skLineSegment(sketch, "E92.MirrorCS", {"start": v(15, -120) * mm, "end": v(15, -108) * mm});
            skLineSegment(sketch, "E93.MirrorCS", {"start": v(-15, -120) * mm, "end": v(-15, -108) * mm});
            skCircle(sketch, "E94.MirrorC", {"center": v(0, -120) * mm, "radius": 6 * mm});
            skLineSegment(sketch, "E95.MirrorCS", {"start": v(0, -90) * mm, "end": v(0, -120) * mm, "construction": true});
            skSolve(sketch);
        }
        {
            var Q0;
            Q0 = qSketchRegion(id + "F16", true);
            var Q1;
            Q1=makeQuery(id+"F2.opExtrude","CAP_FACE",FACE,{"disambiguationData":[OSD([sQuery(id+"F0.wireOp",EDGE,"E12"),sQuery(id+"F0.wireOp",EDGE,"E13"),sQuery(id+"F0.wireOp",EDGE,"E14"),sQuery(id+"F0.wireOp",EDGE,"E15"),sQuery(id+"F0.wireOp",EDGE,"E17.filletArc"),sQuery(id+"F0.wireOp",EDGE,"E18.filletArc"),sQuery(id+"F0.wireOp",EDGE,"E19.filletArc"),sQuery(id+"F0.wireOp",EDGE,"E20.filletArc"),sQuery(id+"F0.wireOp",EDGE,"E25.0"),sQuery(id+"F0.wireOp",EDGE,"E25.1"),sQuery(id+"F0.wireOp",EDGE,"E25.2"),sQuery(id+"F0.wireOp",EDGE,"E25.3"),sQuery(id+"F0.wireOp",EDGE,"E25.4"),sQuery(id+"F0.wireOp",EDGE,"E25.5"),sQuery(id+"F0.wireOp",EDGE,"E25.6"),sQuery(id+"F0.wireOp",EDGE,"E25.7")])],"isStart":false});
            extrude(context, id + "F17", {"entities" : qUnion([Q0]), "endBound" : BoundingType.UP_TO_SURFACE, "endBoundEntityFace" : qUnion([Q1]), "depth" : 25 * mm});
        }
    });
